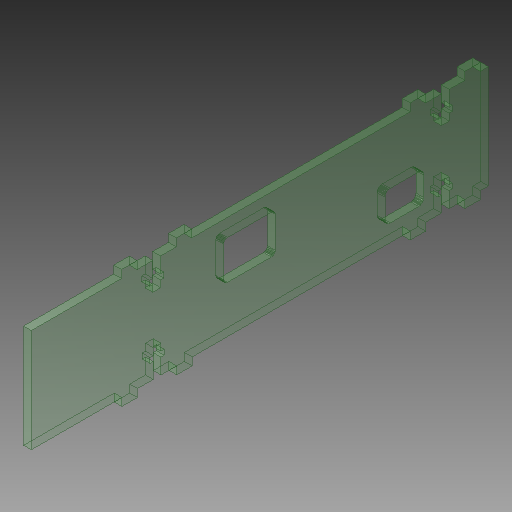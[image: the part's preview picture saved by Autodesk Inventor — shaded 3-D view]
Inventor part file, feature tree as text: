
AUTODESK INVENTOR PART (.ipt)
format: ipt  version: 2018 (Build 220112000, 112)  size: 289,792 bytes
history: native  units: mm
features: extrude x1, sketch x1
ambient origin geometry x8: Origin, YZ Plane, XZ Plane, XY Plane, X Axis, Y Axis, Z Axis, Center Point
bodies: Solid1 (feature_tree)
feature tree (2):
  extrude  "Extrusion1"  [1 undecoded]
  sketch  "Sketch1"  dims[d0=3.0mm d1=0.0mm]
note: 1 required parameter value undecoded (feature->parameter linkage not recoverable at this tier; creation-order binding heuristic only, values carry confidence <= 0.55)
